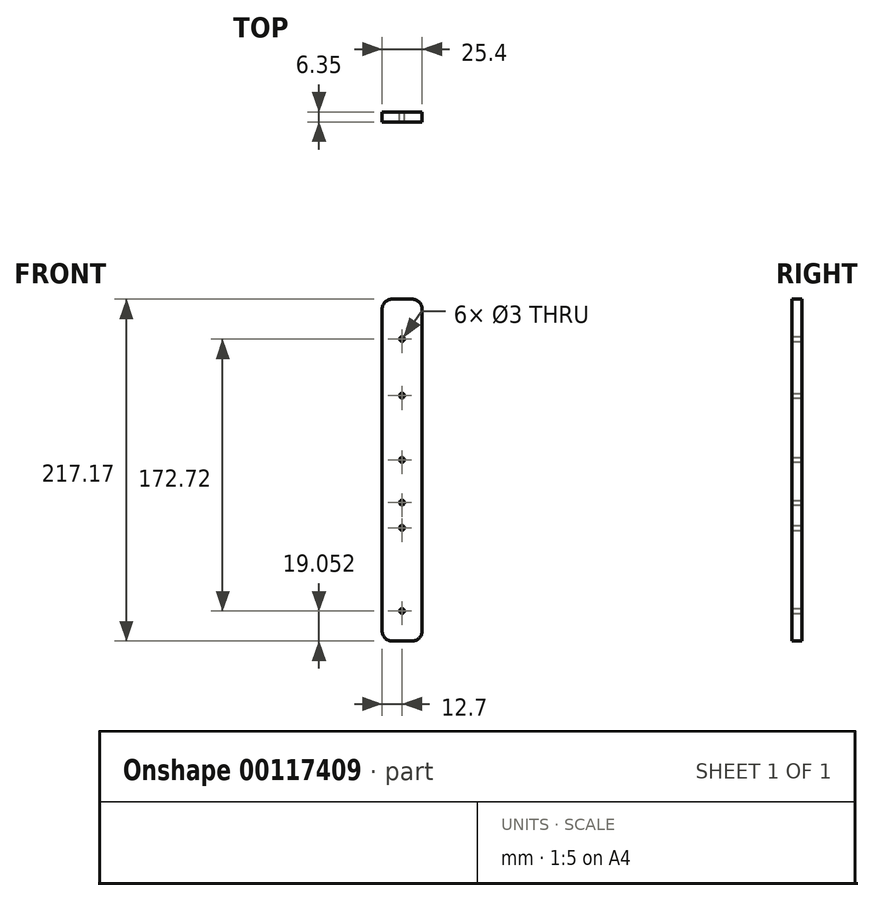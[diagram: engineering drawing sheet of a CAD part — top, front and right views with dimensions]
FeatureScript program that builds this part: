
annotation { "Feature Type Name" : "Feature", "Feature Type Description" : "" }
export const myFeature = defineFeature(function(context is Context, id is Id, definition is map)
    precondition{}
    {
        {
            var Q0;
            Q0=qCreatedBy(makeId("Front.planeOp"),FACE);
            var sketch = newSketch(context, id + "F0", { "sketchPlane" : qUnion([Q0])});
            skCircle(sketch, "E0", {"center": v(0, -84.35) * mm, "radius": 1.5 * mm});
            skCircle(sketch, "E1", {"center": v(0, -31.54) * mm, "radius": 1.5 * mm});
            skCircle(sketch, "E2", {"center": v(0, -15.54) * mm, "radius": 1.5 * mm});
            skCircle(sketch, "E3", {"center": v(0, 11.66) * mm, "radius": 1.5 * mm});
            skCircle(sketch, "E4", {"center": v(0, 88.37) * mm, "radius": 1.5 * mm});
            skLineSegment(sketch, "E5.bottom", {"start": v(-6.35, 113.77) * mm, "end": v(6.35, 113.77) * mm});
            skLineSegment(sketch, "E5.top", {"start": v(-6.35, -103.4) * mm, "end": v(6.35, -103.4) * mm});
            skLineSegment(sketch, "E5.left", {"start": v(-12.7, 107.42) * mm, "end": v(-12.7, -97.05) * mm});
            skLineSegment(sketch, "E5.right", {"start": v(12.7, 107.42) * mm, "end": v(12.7, -97.05) * mm});
            skPoint(sketch, "E6.visualSharp", {"position": v(12.7, 113.77) * mm});
            skArc(sketch, "E6.filletArc", {"start": v(12.7, 107.42) * mm, "mid": v(10.84, 111.91) * mm, "end": v(6.35, 113.77) * mm});
            skPoint(sketch, "E7.visualSharp", {"position": v(-12.7, 113.77) * mm});
            skArc(sketch, "E7.filletArc", {"start": v(-6.35, 113.77) * mm, "mid": v(-10.84, 111.91) * mm, "end": v(-12.7, 107.42) * mm});
            skPoint(sketch, "E8.visualSharp", {"position": v(12.7, -103.4) * mm});
            skArc(sketch, "E8.filletArc", {"start": v(6.35, -103.4) * mm, "mid": v(10.84, -101.54) * mm, "end": v(12.7, -97.05) * mm});
            skPoint(sketch, "E9.visualSharp", {"position": v(-12.7, -103.4) * mm});
            skArc(sketch, "E9.filletArc", {"start": v(-12.7, -97.05) * mm, "mid": v(-10.84, -101.54) * mm, "end": v(-6.35, -103.4) * mm});
            skCircle(sketch, "E10", {"center": v(0, 52.46) * mm, "radius": 1.5 * mm});
            skSolve(sketch);
        }
        {
            var Q0;
            Q0=makeQuery(id+"F0.imprint","IMPRINT",FACE,{"disambiguationData":[TD([[makeQuery(id+"F0.imprint","IMPRINT",EDGE,{"derivedFrom":sQuery(id+"F0.wireOp",EDGE,"E0")}),-1.0]])]});
            extrude(context, id + "F1", {"entities" : qUnion([Q0]), "depth" : 6.35 * mm});
        }
    });
